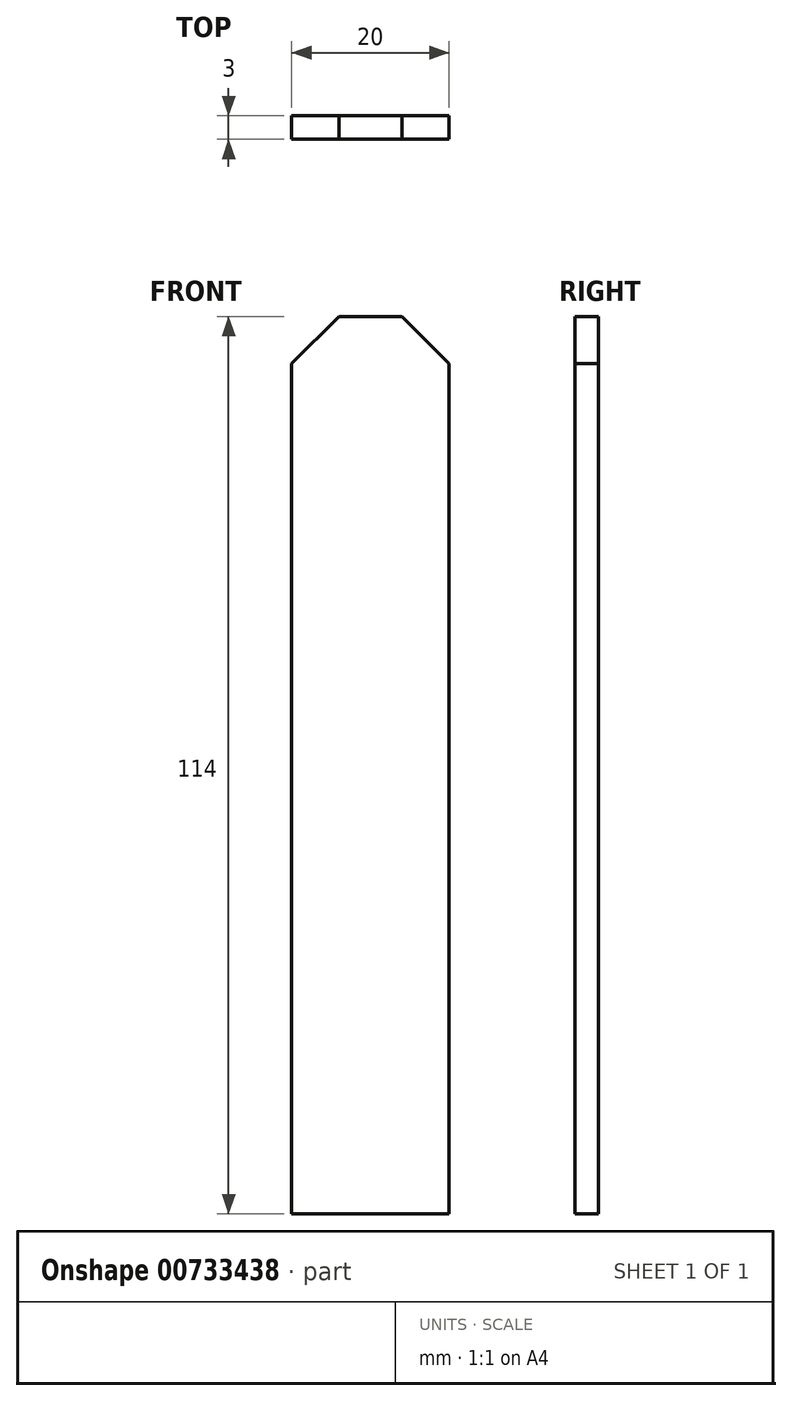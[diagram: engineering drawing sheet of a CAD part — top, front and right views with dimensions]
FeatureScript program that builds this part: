
annotation { "Feature Type Name" : "Feature", "Feature Type Description" : "" }
export const myFeature = defineFeature(function(context is Context, id is Id, definition is map)
    precondition{}
    {
        {
            var Q0;
            Q0=qCreatedBy(makeId("Front.planeOp"),FACE);
            var sketch = newSketch(context, id + "F0", { "sketchPlane" : qUnion([Q0])});
            skLineSegment(sketch, "E0.bottom", {"start": v(10, 57) * mm, "end": v(-10, 57) * mm});
            skLineSegment(sketch, "E0.top", {"start": v(10, -57) * mm, "end": v(-10, -57) * mm});
            skLineSegment(sketch, "E0.left", {"start": v(10, 57) * mm, "end": v(10, -57) * mm});
            skLineSegment(sketch, "E0.right", {"start": v(-10, 57) * mm, "end": v(-10, -57) * mm});
            skPoint(sketch, "E0.middle", {"position": v(0, 0) * mm});
            skSolve(sketch);
        }
        {
            var Q0;
            Q0=makeQuery(id+"F0.imprint","IMPRINT",FACE,{"disambiguationData":[TD([[makeQuery(id+"F0.imprint","IMPRINT",EDGE,{"derivedFrom":sQuery(id+"F0.wireOp",EDGE,"E0.bottom")}),1.0]])]});
            extrude(context, id + "F1", {"entities" : qUnion([Q0]), "depth" : 3 * mm, "offsetDistance" : 25 * mm});
        }
        {
            var Q0;
            Q0=makeQuery(id+"F1.opExtrude","SWEPT_EDGE",EDGE,{"disambiguationData":[OSD([sQuery(id+"F0.wireOp",EDGE,"E0.bottom"),sQuery(id+"F0.wireOp",EDGE,"E0.left")])]});
            var Q1;
            Q1=makeQuery(id+"F1.opExtrude","SWEPT_EDGE",EDGE,{"disambiguationData":[OSD([sQuery(id+"F0.wireOp",EDGE,"E0.bottom"),sQuery(id+"F0.wireOp",EDGE,"E0.right")])]});
            chamfer(context, id + "F2", {"entities" : qUnion([Q0, Q1]), "width" : 6 * mm, "tangentPropagation" : true});
        }
    });
